# Revit family: Digital_Media-Honeywell-Power_Supply-581722(3)
name_source: partatom
category: Electrical Equipment
revit_build: Autodesk Revit 2017 (Build: 20160225_1515(x64)
units: mm (PartAtom-declared; Revit-internal decimal feet)

## family parameters
Cut with Voids When Loaded = No
Host = Face
OmniClass Number = 23.85.50.00
OmniClass Title = Communication Systems
Part Type = Equipment Switch
Room Calculation Point = No
Round Connector Dimension = Use Diameter
Shared = No

## types (2) — shared parameters
Ambient Temperature = -5 °C ... 40 °C
Apparent Load = 230 VA
Default Elevation = 1219 mm
Depth = 328 mm  [stored 1.07612 ft]
Finish = Metal - Honeywell - Stainless Steel - Black
Frequency = 50 Hz
Load Sub-Classification = No
Manufacturer = Honeywell International
Manufacturer Fax Number = 02131/40615-606
Number of Poles = 1
Power Factor = 1
Product Documentation Link = https://www.esser-systems.com
Product Page URL = https://www.esser-systems.com
Rated Frequency = 50 ... 60 Hz
Rated Voltage = 230 V AC
Storage Temperature = -40 °C ... 85 °C
URL = www.esser-systems.com
Utility = No
Version = 2017 - v1.0a
Voltage = 230
Watts = 0 W
Width = 483 mm

## per-type parameters (varying)
| type | Battery Capacity | Constraints | Description | Height | Model | Output Current | Product Name | Weight |
| PSU 24 V-4 - 581723 | max. 640 Ah | 1 | Emergency power supply PSU 24 V42 | 89 mm  [stored 0.291995 ft] | 581723 | max. 372 A (battery) | PSU 24 V-4 | 8.80 kgf |
| PSU 24 V-2 - 581722 | max. 320 Ah | 2 | Emergency power supply PSU 24 V-2 | 45 mm  [stored 0.147638 ft] | 581722 | max. 186 A (battery) | PSU 24 V-2 | 5.20 kgf |

note: [stored X ft] marks values corroborated as IEEE doubles in the binary element streams (Revit-internal decimal feet)

## geometry (parser evidence)
native form markers: Sweep x3
no freeform markers — native parametric forms only
